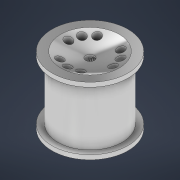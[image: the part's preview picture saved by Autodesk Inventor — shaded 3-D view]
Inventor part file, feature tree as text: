
AUTODESK INVENTOR PART (.ipt)
format: ipt  version: 2021 (Build 250183000, 183)  size: 442,368 bytes
history: native  units: mm
features: other x7, sketch x4, extrude x2
ambient origin geometry x8: Origin, YZ Plane, XZ Plane, XY Plane, X Axis, Y Axis, Z Axis, Center Point
bodies: Body1 (feature_tree)
feature tree (13):
  other  "Roda - Estrutura"
  other  "Sólido1"
  other  "Revolução1"
  other  "Plano de trabalho1"
  extrude  "Extrusão2"  Depth=1.5mm
  other  "Plano de trabalho2"
  extrude  "Extrusão3"  Depth=2.0mm
  other  "Plano de trabalho3"
  other  "Espiral1"
  sketch  "Esboço1"  dims[d0=13.0mm d1=1.5mm]
  sketch  "Esboço3"  dims[d2=2.0mm d3=20.0mm]
  sketch  "Esboço5"  dims[d4=1.5mm]
  sketch  "Esboço6"  dims[d5=13.0mm d8=90.0deg d9=0.0mm d32=30.0mm d34=360.0deg d36=15.0mm d37=0.0mm d38=4.5mm d39=3.0mm d40=12.0mm d41=0.0mm d42=3.0mm d45=0.25mm d46=0.25mm d47=0.5mm d48=10.0mm d49=10.25mm d50=145.0mm d51=0.0mm d52=90.0deg d53=90.0deg d54=0.0mm d55=0.0mm d43=0.872665mm]
